# Revit family: Electronics_Expansion-Inputs_Biamp_Vocia_Input-Device_VI-6__
name_source: partatom
category: Communication Devices
units: mm (PartAtom-declared; Revit-internal decimal feet)

## family parameters
Cut with Voids When Loaded = No
Host = Face
Maintain Annotation Orientation = No
OmniClass Number = 23.85.10.11.14
OmniClass Title = Audio Equipment
Part Type = Normal
Room Calculation Point = No
Round Connector Dimension = Use Diameter
Shared = No

## types (1)
- VI-6
    A/D Converters = 24-bit
    Altitude = 0-10,000 ft (0-3000m) MSL
    Apparent Load = 0 VA
    Compliance = CE marked (Europe); RoHS Directive (Europe)
    Connector Description = PoE IEEE 802.3af Class 0
    Crosstalk = 10kHz: < -75dB
    Default Elevation = 4' - 0"
    Depth = 0' - 10"
    Description = Vocia® VI-6 Input Device
    Dynamic Range = >100dB
    Frequency Response Line Inputs = 20Hz to 20kHz: ± 1dB
    Frequency Response Mic/Line Inputs = 35Hz to 20kHz: ± 1dB
    Height = 0' - 1 1/2"
    Housing Material = Biamp - Metal - Silver
    Humidity = 0-95% relative humidity (non-condensing)
    Input Impedance = 100kOhm
    Input Impedance Line Inputs = >10kOhm
    Input Impedance Mic/Line Inputs = >1kOhm
    Line Inputs Signal to Noise Ratio = >84dB
    Manufacturer = Biamp
    Max Input Threshold = 10V
    Max Input Voltage = 12V
    Max Operating Voltage = 125VAC, 60VDC
    Max Power Consumption = 0 W
    Max Switching Capacity = 37VA
    Mic Inputs Equivalent Input Noise = <-126dBu
    Mic Inputs Phantom Power = 18V behind 3.3kOhm/leg
    Min Input Threshold = 150mV
    Min Operating Load = 10µA at 10mV DC
    Model = Vocia VI-6
    Network Connection = Dual RJ45 with shielded Ethernet (CAT5, CAT5e, CAT6, or CAT7)
    Number of Poles = 1
    Power Factor = 1
    Product Documentation Link = https://downloads.biamp.com
    Product Page URL = https://www.biamp.com
    Product data url = https://www.bimobject.com
    Sample Rate = 48kHz
    THD+N Line Inputs = 20Hz to 8kHz: <0.02%
    THD+N Mic/Line Inputs = 20Hz to 8kHz: <0.05%
    Temperature Range = 23 - 104° F (-5 – 40° C)
    Type Control Inputs = Digital, variable threshold
    Type Control Outputs = Form C Voltage free change over contact
Form C Voltage free change over contact
    URL = https://www.biamp.com
    Voltage = 0 V
    Weight = 6.40 lbf
    Width = 1' - 7"

## geometry (parser evidence)
native form markers: Sweep x2
no freeform markers — native parametric forms only
